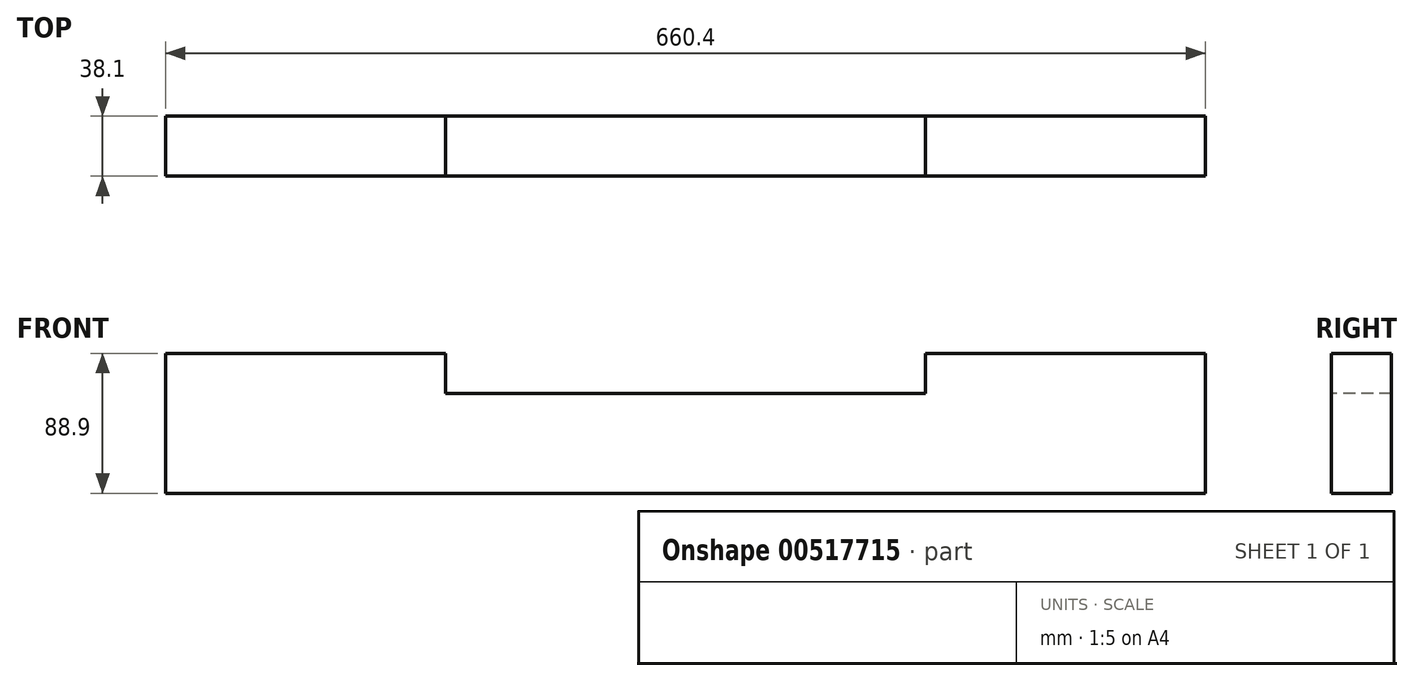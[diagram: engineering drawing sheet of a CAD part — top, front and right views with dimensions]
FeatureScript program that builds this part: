
annotation { "Feature Type Name" : "Feature", "Feature Type Description" : "" }
export const myFeature = defineFeature(function(context is Context, id is Id, definition is map)
    precondition{}
    {
        {
            var Q0;
            Q0=qCreatedBy(makeId("Front.planeOp"),FACE);
            var sketch = newSketch(context, id + "F0", { "sketchPlane" : qUnion([Q0])});
            skLineSegment(sketch, "E0.bottom", {"start": v(330.2, 44.45) * mm, "end": v(-330.2, 44.45) * mm});
            skLineSegment(sketch, "E0.top", {"start": v(330.2, -44.45) * mm, "end": v(-330.2, -44.45) * mm});
            skLineSegment(sketch, "E0.left", {"start": v(330.2, 44.45) * mm, "end": v(330.2, -44.45) * mm});
            skLineSegment(sketch, "E0.right", {"start": v(-330.2, 44.45) * mm, "end": v(-330.2, -44.45) * mm});
            skPoint(sketch, "E0.middle", {"position": v(0, 0) * mm});
            skSolve(sketch);
        }
        {
            var Q0;
            Q0=makeQuery(id+"F0.imprint","IMPRINT",FACE,{"disambiguationData":[TD([[makeQuery(id+"F0.imprint","IMPRINT",EDGE,{"derivedFrom":sQuery(id+"F0.wireOp",EDGE,"E0.bottom")}),1.0]])]});
            extrude(context, id + "F1", {"entities" : qUnion([Q0]), "depth" : 38.1 * mm, "offsetDistance" : 25.4 * mm});
        }
        {
            var Q0;
            Q0=makeQuery(id+"F1.opExtrude","SWEPT_FACE",FACE,{"disambiguationData":[OSD([sQuery(id+"F0.wireOp",EDGE,"E0.bottom")])]});
            var sketch = newSketch(context, id + "F2", { "sketchPlane" : qUnion([Q0])});
            skLineSegment(sketch, "E1.bottom", {"start": v(-152.4, 0) * mm, "end": v(152.4, 0) * mm});
            skLineSegment(sketch, "E1.top", {"start": v(-152.4, -38.1) * mm, "end": v(152.4, -38.1) * mm});
            skLineSegment(sketch, "E1.left", {"start": v(-152.4, 0) * mm, "end": v(-152.4, -38.1) * mm});
            skLineSegment(sketch, "E1.right", {"start": v(152.4, 0) * mm, "end": v(152.4, -38.1) * mm});
            skSolve(sketch);
        }
        {
            var Q0;
            Q0=makeQuery(id+"F2.imprint","IMPRINT",FACE,{"disambiguationData":[TD([[makeQuery(id+"F2.imprint","IMPRINT",EDGE,{"derivedFrom":sQuery(id+"F2.wireOp",EDGE,"E1.bottom")}),1.0]])]});
            extrude(context, id + "F3", {"entities" : qUnion([Q0]), "operationType" : NewBodyOperationType.REMOVE, "oppositeDirection" : true, "depth" : 25.4 * mm, "offsetDistance" : 25.4 * mm});
        }
    });
